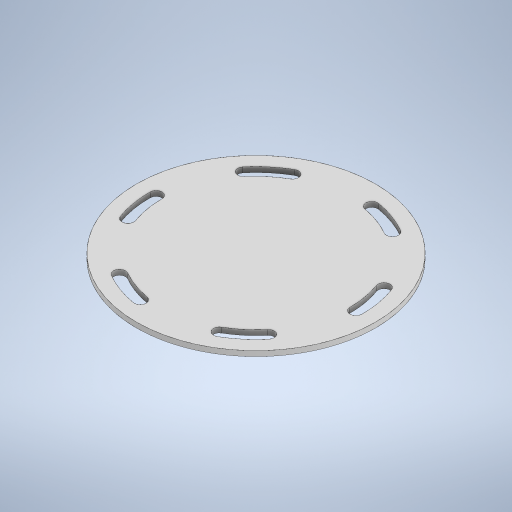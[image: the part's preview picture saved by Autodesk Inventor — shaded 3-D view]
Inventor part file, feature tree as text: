
AUTODESK INVENTOR PART (.ipt)
format: ipt  version: 2024.3 (Build 283343000, 343)  size: 253,440 bytes
history: native  units: mm
features: extrude x2, sketch x2, pattern_circular x1
ambient origin geometry x8: Origin, YZ Plane, XZ Plane, XY Plane, X Axis, Y Axis, Z Axis, Center Point
bodies: Solid1 (feature_tree)
feature tree (5):
  extrude  "Extrusion1"  Depth=3.0mm TaperAngle=0.0deg
  extrude  "Extrusion2"  Depth=110.0mm
  pattern_circular  "Circular Pattern1"  Count=2  [1 undecoded]
  sketch  "Sketch1"  dims[d0=140.0mm d1=3.0mm d2=0.0mm]
  sketch  "Sketch2"  dims[d3=124.0mm d4=110.0mm d7=20.0mm d8=0.0mm d9=0.0mm d10=60.0mm d11=360.0deg]
note: 1 required parameter value undecoded (feature->parameter linkage not recoverable at this tier; creation-order binding heuristic only, values carry confidence <= 0.55)
